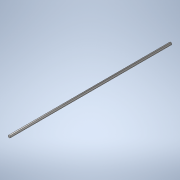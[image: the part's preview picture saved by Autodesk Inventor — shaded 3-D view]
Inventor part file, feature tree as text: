
AUTODESK INVENTOR PART (.ipt)
format: ipt  version: 2020 (Build 240168000, 168)  size: 110,592 bytes
history: native  units: in
note: dims shown in document units (in); Inventor stores cm internally (conversion verified against a paired STEP export)
features: extrude x1, sketch x1
ambient origin geometry x8: Origin, YZ Plane, XZ Plane, XY Plane, X Axis, Y Axis, Z Axis, Center Point
bodies: Solid1 (feature_tree)
feature tree (2):
  extrude  "Extrusion1"  Depth=39.0in TaperAngle=0.0deg
  sketch  "Sketch1"  dims[d0=0.5in d1=39.0in d2=0.0in]
